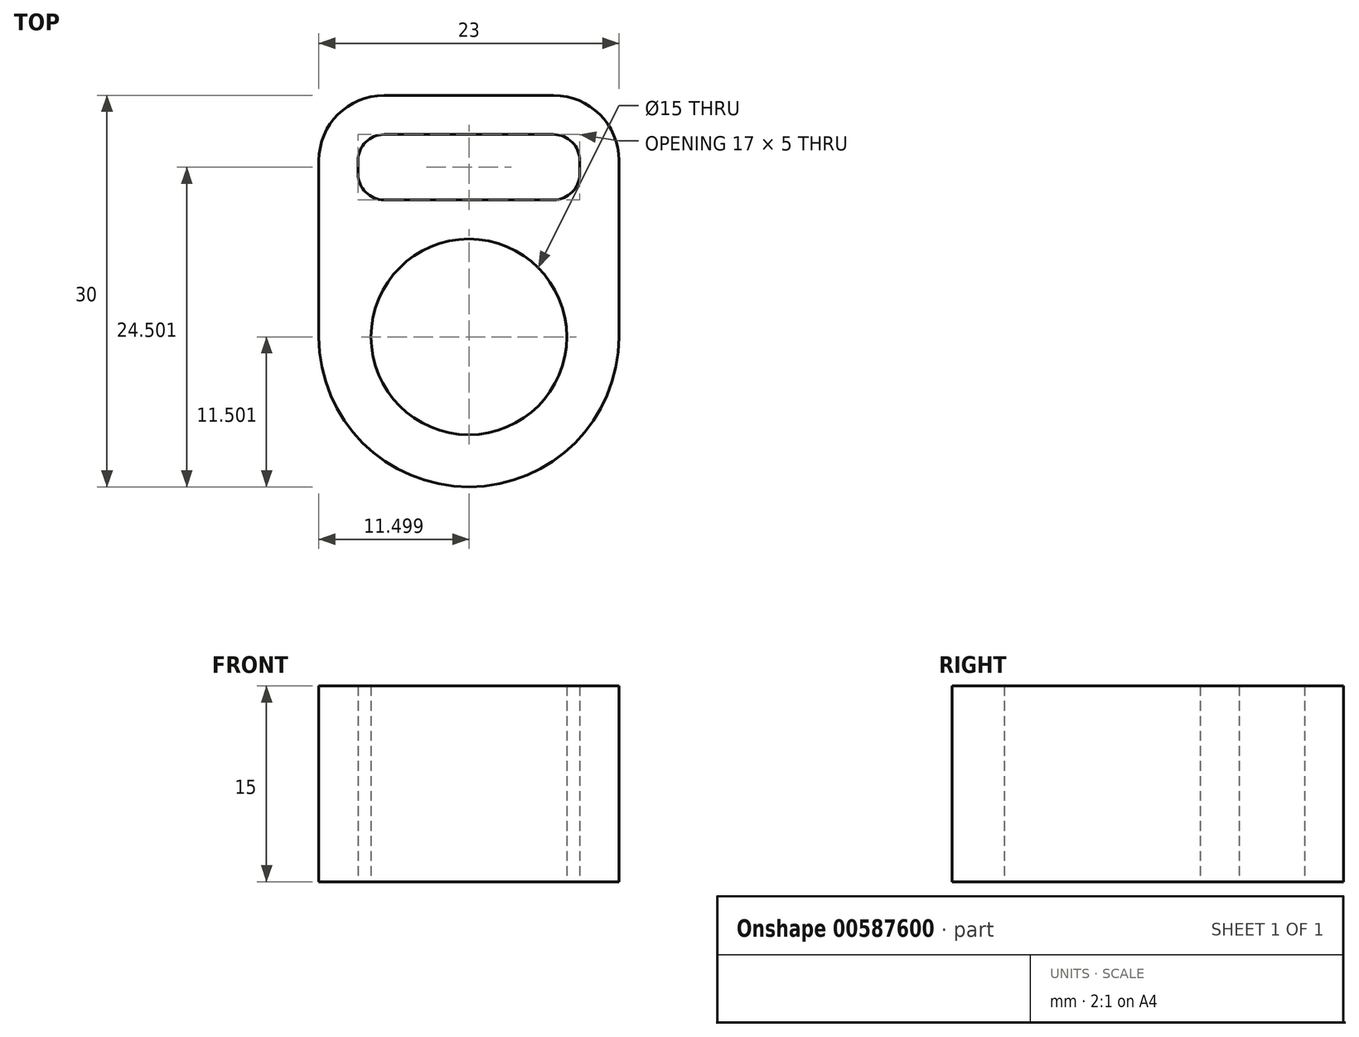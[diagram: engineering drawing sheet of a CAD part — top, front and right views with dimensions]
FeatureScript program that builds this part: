
annotation { "Feature Type Name" : "Feature", "Feature Type Description" : "" }
export const myFeature = defineFeature(function(context is Context, id is Id, definition is map)
    precondition{}
    {
        {
            var Q0;
            Q0=qCreatedBy(makeId("Top.planeOp"),FACE);
            var sketch = newSketch(context, id + "F0", { "sketchPlane" : qUnion([Q0])});
            skLineSegment(sketch, "E0.bottom", {"start": v(-98.88, 43.68) * mm, "end": v(-85.88, 43.68) * mm});
            skLineSegment(sketch, "E0.top", {"start": v(-98.88, 38.68) * mm, "end": v(-85.88, 38.68) * mm});
            skLineSegment(sketch, "E0.left", {"start": v(-100.88, 41.68) * mm, "end": v(-100.88, 40.68) * mm});
            skLineSegment(sketch, "E0.right", {"start": v(-83.88, 41.68) * mm, "end": v(-83.88, 40.68) * mm});
            skPoint(sketch, "E1.visualSharp", {"position": v(-100.88, 43.68) * mm});
            skArc(sketch, "E1.filletArc", {"start": v(-98.88, 43.68) * mm, "mid": v(-100.3, 43.1) * mm, "end": v(-100.88, 41.68) * mm});
            skPoint(sketch, "E2.visualSharp", {"position": v(-100.88, 38.68) * mm});
            skArc(sketch, "E2.filletArc", {"start": v(-100.88, 40.68) * mm, "mid": v(-100.3, 39.27) * mm, "end": v(-98.88, 38.68) * mm});
            skPoint(sketch, "E3.visualSharp", {"position": v(-83.88, 38.68) * mm});
            skArc(sketch, "E3.filletArc", {"start": v(-85.88, 38.68) * mm, "mid": v(-84.47, 39.27) * mm, "end": v(-83.88, 40.68) * mm});
            skPoint(sketch, "E4.visualSharp", {"position": v(-83.88, 43.68) * mm});
            skArc(sketch, "E4.filletArc", {"start": v(-83.88, 41.68) * mm, "mid": v(-84.47, 43.1) * mm, "end": v(-85.88, 43.68) * mm});
            skLineSegment(sketch, "E5.0", {"start": v(-98.88, 46.68) * mm, "end": v(-85.88, 46.68) * mm});
            skArc(sketch, "E5.1", {"start": v(-80.88, 41.68) * mm, "mid": v(-82.35, 45.22) * mm, "end": v(-85.88, 46.68) * mm});
            skArc(sketch, "E5.2", {"start": v(-98.88, 46.68) * mm, "mid": v(-102.42, 45.22) * mm, "end": v(-103.88, 41.68) * mm});
            skLineSegment(sketch, "E5.3", {"start": v(-80.88, 41.68) * mm, "end": v(-80.88, 40.68) * mm});
            skLineSegment(sketch, "E5.4", {"start": v(-103.88, 41.68) * mm, "end": v(-103.88, 40.68) * mm});
            skCircle(sketch, "E6", {"center": v(-92.38, 28.18) * mm, "radius": 7.5 * mm});
            skPoint(sketch, "E6.centerSnap0", {"position": v(-92.38, 38.68) * mm});
            skLineSegment(sketch, "E7", {"start": v(-80.88, 40.68) * mm, "end": v(-80.88, 28.18) * mm});
            skLineSegment(sketch, "E8", {"start": v(-103.88, 40.68) * mm, "end": v(-103.88, 28.18) * mm});
            skArc(sketch, "E9", {"start": v(-103.88, 28.18) * mm, "mid": v(-92.38, 16.68) * mm, "end": v(-80.88, 28.18) * mm});
            skSolve(sketch);
        }
        {
            var Q0;
            Q0 = qSketchRegion(id + "F0", true);
            extrude(context, id + "F1", {"entities" : qUnion([Q0]), "depth" : 15 * mm, "offsetDistance" : 25 * mm});
        }
    });
